# Revit family: Hager-Madrid-IP65-D250-Cl.I-Steel_encl-630A-IT-it
name_source: partatom
category: Equipement électrique
units: mm (PartAtom-declared; Revit-internal decimal feet)

## family parameters
Configuration du panneau = Deux colonnes, circuits au sein
Cote de connecteur circulaire = Utiliser le diamètre
Couper avec des vides une fois chargée = Non
Hôte = Face
Partagée = Non
Point de calcul de pièce = Non
Type d'élément = Tableau de raccordement

## types (11) — shared parameters
Commentaires du type = Madrid
EF000003 - Tipo di montaggio = EV000384 - A parete
EF000007 - colore = EV000270 - grigio
EF000049 - profondità = 250 mm  [stored 0.82021 ft]
EF000116 - numero RAL = 7035
EF000118 - con piastra di montaggio = Oui
EF000339 - tipo di copertura = EV004216 - porta
EF001088 - possibilità di applicazione = Oui
EF001131 - profondità interna = 250 mm  [stored 0.82021 ft]
EF001596 - Attacco Lampada = EV000179 - acciaio
EF001613 - Integrità del circuito = EV000494 - senza
EF003532 - adatto per uso esterno = Non
EF004293 - resistenza agli urti = EV008784 - IK10
EF004464 - tipo di porta = EV002646 - singolo
EF005474 - grado di protezione (IP) = EV006421 - IP65
EF007800 - adatto per parafulmine = Non
EF008873 - corrente nominale (In) = 630 A
EF009170 - spessore materiale scatola = 1 mm  [stored 0.00328084 ft]
EF009171 - spessore materiale porta/coperchio = 2 mm  [stored 0.00656168 ft]
EF009212 - esecuzione coperchio = EV000116 - chiuso
EF015940 - Coprire con rilascio di sovrapressione = Non
Fabricant = Hager
HG000002 - Con porta = Oui
HG000003 - Gamma = Madrid
HG000006 - Ad incasso = Non
HG000009 - Porta doppia a battente = Non
HG000010 - Porte asimmetriche = Non
HG000023 - Custodia a doppia sezione = Non
HG000024 - Altezza della sezione inferiore = 800 mm  [stored 2.62467 ft]
HG000026 - A pavimento = Non
zero-valued in all types: EF000218 - profondità di incasso, EF002950 - Numero moduli DIN, EF004427 - numero di moduli, Elévation par défaut, HG000027 - Altezza dello zoccolo

## per-type parameters (varying)
| type | EF000008 - Larghezza | EF000040 - Altezza | EF000266 - numero di file | EF000437 - numero di ingressi per conduttori | EF006244 - coperchio/porta trasparente | EF006306 - con serratura | EF009554 - numero delle aperture per la piastra della flangia | HG000004 - Codice produttore |
| A parete IP65 L400 A600 P250  - 35715 | 400 mm  [stored 1.31234 ft] | 600 mm | 0 | 0 | Non | Oui | 0 | 35715 |
| A parete IP65 L400 A600 P250  - 35765 | 400 mm  [stored 1.31234 ft] | 600 mm | 0 | 2 | Oui | Non | 2 | 35765 |
| A parete IP65 L500 A650 P250  - 35721 | 500 mm  [stored 1.64042 ft] | 650 mm | 1 | 2 | Non | Oui | 2 | 35721 |
| A parete IP65 L500 A650 P250  - 35771 | 500 mm  [stored 1.64042 ft] | 650 mm | 4 | 2 | Oui | Non | 2 | 35771 |
| A parete IP65 L600 A1250 P250  - 35739 | 600 mm | 1250 mm | 8 | 2 | Non | Oui | 2 | 35739 |
| A parete IP65 L600 A1250 P250  - 35789 | 600 mm | 1250 mm | 8 | 2 | Oui | Non | 2 | 35789 |
| A parete IP65 L600 A600 P250  - 35717 | 600 mm | 600 mm | 0 | 2 | Non | Oui | 2 | 35717 |
| A parete IP65 L600 A600 P250  - 35767 | 600 mm | 600 mm | 0 | 2 | Oui | Non | 2 | 35767 |
| A parete IP65 L600 A800 P250  - 35728 | 600 mm | 800 mm  [stored 2.62467 ft] | 1 | 2 | Non | Oui | 2 | 35728 |
| A parete IP65 L600 A800 P250  - 35778 | 600 mm | 800 mm  [stored 2.62467 ft] | 5 | 2 | Oui | Non | 2 | 35778 |
| A parete IP65 L800 A950 P250  - 35736 | 800 mm  [stored 2.62467 ft] | 950 mm  [stored 3.1168 ft] | 1 | 2 | Non | Oui | 2 | 35736 |

note: [stored X ft] marks values corroborated as IEEE doubles in the binary element streams (Revit-internal decimal feet)

## geometry (parser evidence)
native form markers: Sweep x7
no freeform markers — native parametric forms only
